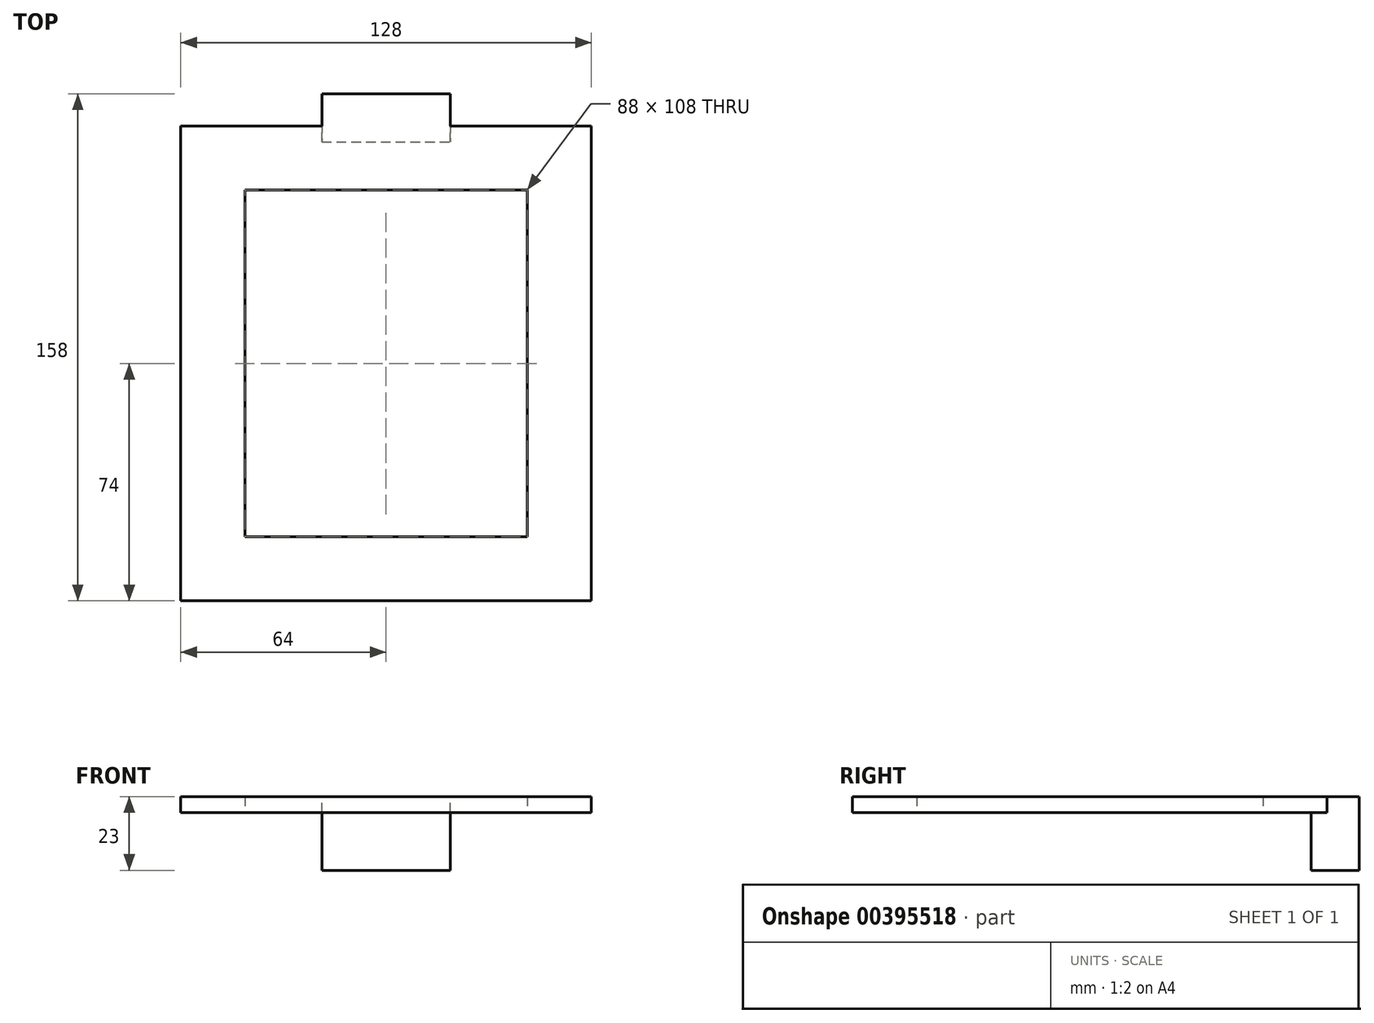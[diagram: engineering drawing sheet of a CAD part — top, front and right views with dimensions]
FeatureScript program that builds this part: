
annotation { "Feature Type Name" : "Feature", "Feature Type Description" : "" }
export const myFeature = defineFeature(function(context is Context, id is Id, definition is map)
    precondition{}
    {
        {
            assignVariable(context, id + "F0", {"name" : "GuideBushDiameter", "anyValue" : 17 * mm});
        }
        {
            assignVariable(context, id + "F1", {"name" : "BitDiameter", "anyValue" : 7 * mm});
        }
        {
            assignVariable(context, id + "F2", {"name" : "Height", "anyValue" : 5 * mm});
        }
        {
            var Q0;
            Q0=qCreatedBy(makeId("Top.planeOp"),FACE);
            var sketch = newSketch(context, id + "F3", { "sketchPlane" : qUnion([Q0])});
            skLineSegment(sketch, "E0.bottom", {"start": v(39, 49) * mm, "end": v(-39, 49) * mm, "construction": true});
            skLineSegment(sketch, "E0.top", {"start": v(39, -49) * mm, "end": v(-39, -49) * mm, "construction": true});
            skLineSegment(sketch, "E0.left", {"start": v(39, 49) * mm, "end": v(39, -49) * mm, "construction": true});
            skLineSegment(sketch, "E0.right", {"start": v(-39, 49) * mm, "end": v(-39, -49) * mm, "construction": true});
            skPoint(sketch, "E0.middle", {"position": v(0, 0) * mm});
            skLineSegment(sketch, "E1.bottom", {"start": v(-44, 54) * mm, "end": v(44, 54) * mm});
            skLineSegment(sketch, "E1.top", {"start": v(-44, -54) * mm, "end": v(44, -54) * mm});
            skLineSegment(sketch, "E1.left", {"start": v(-44, 54) * mm, "end": v(-44, -54) * mm});
            skLineSegment(sketch, "E1.right", {"start": v(44, 54) * mm, "end": v(44, -54) * mm});
            skLineSegment(sketch, "E2.bottom", {"start": v(64, 74) * mm, "end": v(-64, 74) * mm});
            skLineSegment(sketch, "E2.top", {"start": v(64, -74) * mm, "end": v(-64, -74) * mm});
            skLineSegment(sketch, "E2.left", {"start": v(64, 74) * mm, "end": v(64, -74) * mm});
            skLineSegment(sketch, "E2.right", {"start": v(-64, 74) * mm, "end": v(-64, -74) * mm});
            skSolve(sketch);
        }
        {
            var Q0;
            Q0 = qSketchRegion(id + "F3", true);
            extrude(context, id + "F4", {"entities" : qUnion([Q0]), "depth" : getVariable(context, 'Height')});
        }
        {
            var Q0;
            Q0=makeQuery(id+"F4.opExtrude","SWEPT_FACE",FACE,{"disambiguationData":[OSD([sQuery(id+"F3.wireOp",EDGE,"E2.bottom")])]});
            var sketch = newSketch(context, id + "F5", { "sketchPlane" : qUnion([Q0])});
            skLineSegment(sketch, "E3.bottom", {"start": v(-20, 0) * mm, "end": v(20, 0) * mm});
            skLineSegment(sketch, "E3.top", {"start": v(-20, 5) * mm, "end": v(20, 5) * mm});
            skLineSegment(sketch, "E3.left", {"start": v(-20, 0) * mm, "end": v(-20, 5) * mm});
            skLineSegment(sketch, "E3.right", {"start": v(20, 0) * mm, "end": v(20, 5) * mm});
            skSolve(sketch);
        }
        {
            var Q0;
            Q0=makeQuery(id+"F5.imprint","IMPRINT",FACE,{"disambiguationData":[TD([[makeQuery(id+"F5.imprint","IMPRINT",EDGE,{"derivedFrom":sQuery(id+"F5.wireOp",EDGE,"E3.bottom")}),1.0]])]});
            extrude(context, id + "F6", {"entities" : qUnion([Q0]), "operationType" : NewBodyOperationType.ADD, "depth" : 10 * mm});
        }
        {
            var Q0;
            Q0=makeQuery(id+"F6.boolean.opBoolean","MERGE",FACE,{"derivedFrom":[makeQuery(id+"F4.opExtrude","CAP_FACE",FACE,{"disambiguationData":[OSD([sQuery(id+"F3.wireOp",EDGE,"E1.bottom"),sQuery(id+"F3.wireOp",EDGE,"E1.top"),sQuery(id+"F3.wireOp",EDGE,"E1.left"),sQuery(id+"F3.wireOp",EDGE,"E1.right"),sQuery(id+"F3.wireOp",EDGE,"E2.bottom"),sQuery(id+"F3.wireOp",EDGE,"E2.top"),sQuery(id+"F3.wireOp",EDGE,"E2.left"),sQuery(id+"F3.wireOp",EDGE,"E2.right")])],"isStart":true}),makeQuery(id+"F6.opExtrude","SWEPT_FACE",FACE,{"disambiguationData":[OSD([sQuery(id+"F5.wireOp",EDGE,"E3.bottom")])]})]});
            var sketch = newSketch(context, id + "F7", { "sketchPlane" : qUnion([Q0])});
            skLineSegment(sketch, "E4.bottom", {"start": v(-20, -74) * mm, "end": v(20, -74) * mm});
            skLineSegment(sketch, "E4.top", {"start": v(-20, -84) * mm, "end": v(20, -84) * mm});
            skLineSegment(sketch, "E4.left", {"start": v(-20, -74) * mm, "end": v(-20, -84) * mm});
            skLineSegment(sketch, "E4.right", {"start": v(20, -74) * mm, "end": v(20, -84) * mm});
            skSolve(sketch);
        }
        {
            var Q0;
            Q0=makeQuery(id+"F7.imprint","IMPRINT",FACE,{"disambiguationData":[TD([[makeQuery(id+"F7.imprint","IMPRINT",EDGE,{"derivedFrom":sQuery(id+"F7.wireOp",EDGE,"E4.bottom")}),-1.0]])]});
            extrude(context, id + "F8", {"entities" : qUnion([Q0]), "operationType" : NewBodyOperationType.ADD, "depth" : 18 * mm});
        }
        {
            var Q0;
            Q0=makeQuery(id+"F8.opExtrude","SWEPT_FACE",FACE,{"disambiguationData":[OSD([sQuery(id+"F7.wireOp",EDGE,"E4.bottom")])]});
            extrude(context, id + "F9", {"entities" : qUnion([Q0]), "operationType" : NewBodyOperationType.ADD, "depth" : (getVariable(context, 'GuideBushDiameter') - getVariable(context, 'BitDiameter')) / 2});
        }
    });
